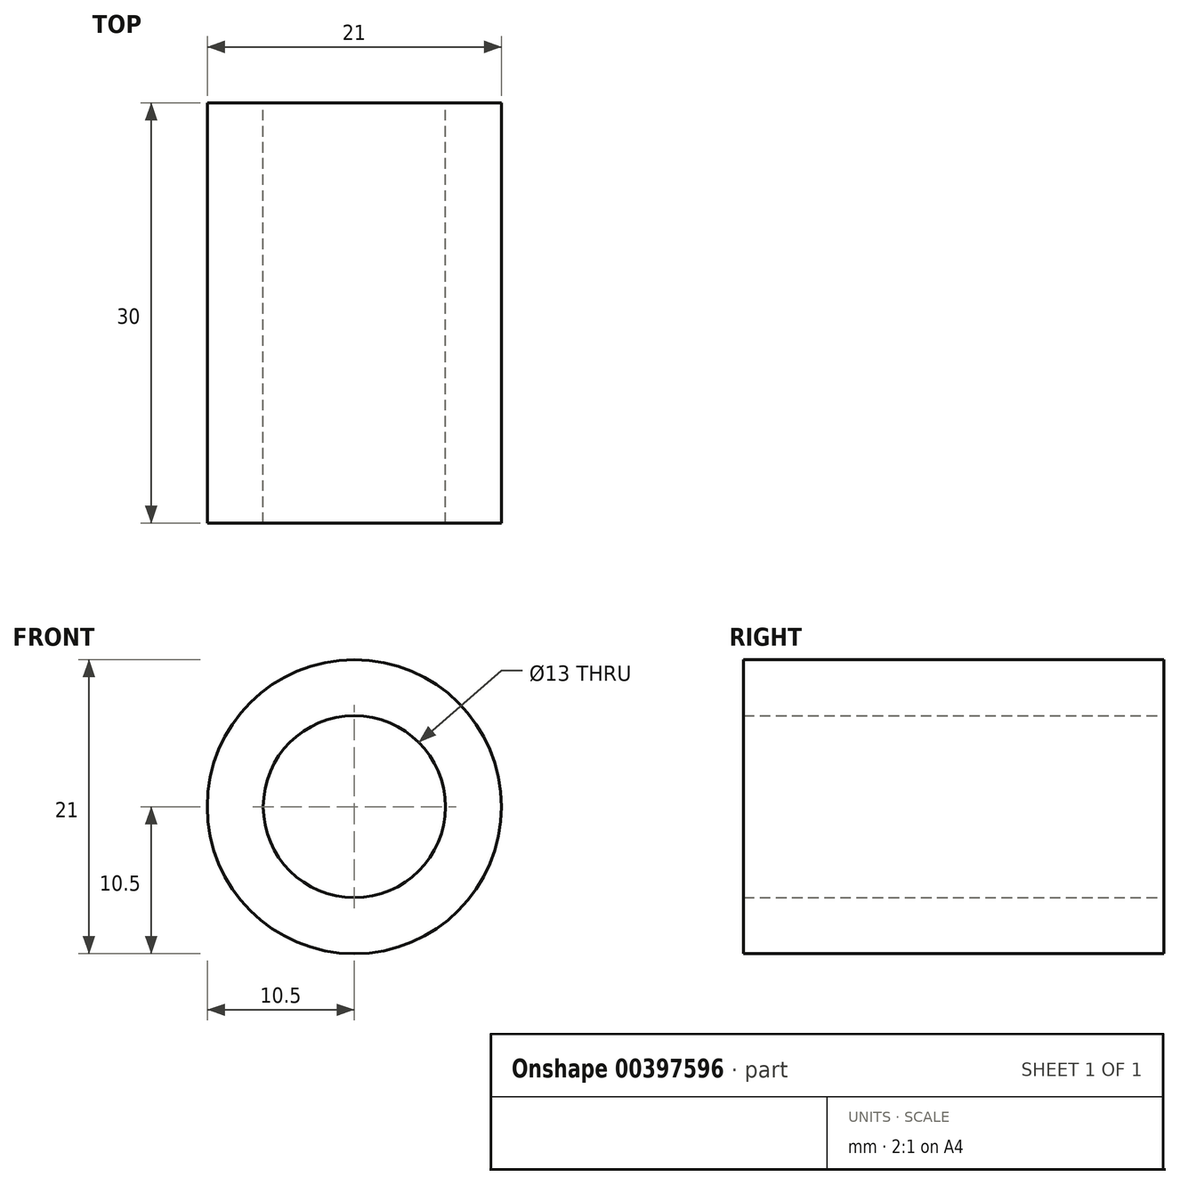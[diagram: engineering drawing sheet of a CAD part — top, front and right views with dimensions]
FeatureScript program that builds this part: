
annotation { "Feature Type Name" : "Feature", "Feature Type Description" : "" }
export const myFeature = defineFeature(function(context is Context, id is Id, definition is map)
    precondition{}
    {
        {
            var Q0;
            Q0=qCreatedBy(makeId("Front.planeOp"),FACE);
            var sketch = newSketch(context, id + "F0", { "sketchPlane" : qUnion([Q0])});
            skCircle(sketch, "E0", {"center": v(0, 0) * mm, "radius": 10.5 * mm});
            skCircle(sketch, "E1", {"center": v(0, 0) * mm, "radius": 6.5 * mm});
            skSolve(sketch);
        }
        {
            var Q0;
            Q0=makeQuery(id+"F0.imprint","IMPRINT",FACE,{"disambiguationData":[TD([[makeQuery(id+"F0.imprint","IMPRINT",EDGE,{"derivedFrom":sQuery(id+"F0.wireOp",EDGE,"E0")}),1.0]])]});
            extrude(context, id + "F1", {"entities" : qUnion([Q0]), "depth" : 30 * mm});
        }
    });
